FCSTD DOCUMENT  (FreeCAD 0.18R16131 (Git))
Label: letterplate_11_11
License: All rights reserved
LicenseURL: http://en.wikipedia.org/wiki/All_rights_reserved
objects: Part::Part2DObjectPython×123, Sketcher::SketchObject×1, PartDesign::Body×1, App::Part×1
note: 125 computed .brp shape members not serialized (recipe doc carries the construction recipe); baked Part::Feature solids carry a one-line shape summary decoded from their .brp

FEATURE [Sketcher::SketchObject] Sketch
  MapMode = 5
  Support = -> [XY_Plane]
FEATURE [PartDesign::Body] Body
  Group = -> [Sketch]
  Origin = -> Origin
FEATURE [Part::Part2DObjectPython] Circle  # Draft 2D object (typed FeaturePython)
  FirstAngle = 0
  LastAngle = 0
  MakeFace = true
  Placement = pos=(115,214.444,0) rot=(0,0,1;0rad)
  Radius = 2.5
FEATURE [Part::Part2DObjectPython] ShapeString  # Draft 2D object (typed FeaturePython)
  FontFile = <userpath>/Dropbox/Hobby/wordclock_git/hardware/lettering_plates/fonts/LiberationMono-Regular-stencil.ttf
  Placement = pos=(27.1303,193.241,0) rot=(0,0,1;0rad)
  Size = 11.4333
  String = H
  Tracking = 0
FEATURE [Part::Part2DObjectPython] ShapeString001  # Draft 2D object (typed FeaturePython)
  FontFile = <userpath>/Dropbox/Hobby/wordclock_git/hardware/lettering_plates/fonts/LiberationMono-Regular-stencil.ttf
  Placement = pos=(43.797,193.241,0) rot=(0,0,1;0rad)
  Size = 11.4333
  String = E
  Tracking = 0
FEATURE [Part::Part2DObjectPython] ShapeString002  # Draft 2D object (typed FeaturePython)
  FontFile = <userpath>/Dropbox/Hobby/wordclock_git/hardware/lettering_plates/fonts/LiberationMono-Regular-stencil.ttf
  Placement = pos=(60.4637,193.241,0) rot=(0,0,1;0rad)
  Size = 11.4333
  String = T
  Tracking = 0
FEATURE [Part::Part2DObjectPython] ShapeString003  # Draft 2D object (typed FeaturePython)
  FontFile = <userpath>/Dropbox/Hobby/wordclock_git/hardware/lettering_plates/fonts/LiberationMono-Regular-stencil.ttf
  Placement = pos=(77.1303,193.241,0) rot=(0,0,1;0rad)
  Size = 11.4333
  String = H
  Tracking = 0
FEATURE [Part::Part2DObjectPython] ShapeString004  # Draft 2D object (typed FeaturePython)
  FontFile = <userpath>/Dropbox/Hobby/wordclock_git/hardware/lettering_plates/fonts/LiberationMono-Regular-stencil.ttf
  Placement = pos=(93.797,193.241,0) rot=(0,0,1;0rad)
  Size = 11.4333
  String = I
  Tracking = 0
FEATURE [Part::Part2DObjectPython] ShapeString005  # Draft 2D object (typed FeaturePython)
  FontFile = <userpath>/Dropbox/Hobby/wordclock_git/hardware/lettering_plates/fonts/LiberationMono-Regular-stencil.ttf
  Placement = pos=(110.464,193.241,0) rot=(0,0,1;0rad)
  Size = 11.4333
  String = S
  Tracking = 0
FEATURE [Part::Part2DObjectPython] ShapeString006  # Draft 2D object (typed FeaturePython)
  FontFile = <userpath>/Dropbox/Hobby/wordclock_git/hardware/lettering_plates/fonts/LiberationMono-Regular-stencil.ttf
  Placement = pos=(127.13,193.241,0) rot=(0,0,1;0rad)
  Size = 11.4333
  String = B
  Tracking = 0
FEATURE [Part::Part2DObjectPython] ShapeString007  # Draft 2D object (typed FeaturePython)
  FontFile = <userpath>/Dropbox/Hobby/wordclock_git/hardware/lettering_plates/fonts/LiberationMono-Regular-stencil.ttf
  Placement = pos=(143.797,193.241,0) rot=(0,0,1;0rad)
  Size = 11.4333
  String = B
  Tracking = 0
FEATURE [Part::Part2DObjectPython] ShapeString008  # Draft 2D object (typed FeaturePython)
  FontFile = <userpath>/Dropbox/Hobby/wordclock_git/hardware/lettering_plates/fonts/LiberationMono-Regular-stencil.ttf
  Placement = pos=(160.464,193.241,0) rot=(0,0,1;0rad)
  Size = 11.4333
  String = Ĳ
  Tracking = 0
FEATURE [Part::Part2DObjectPython] ShapeString009  # Draft 2D object (typed FeaturePython)
  FontFile = <userpath>/Dropbox/Hobby/wordclock_git/hardware/lettering_plates/fonts/LiberationMono-Regular-stencil.ttf
  Placement = pos=(177.13,193.241,0) rot=(0,0,1;0rad)
  Size = 11.4333
  String = N
  Tracking = 0
FEATURE [Part::Part2DObjectPython] ShapeString010  # Draft 2D object (typed FeaturePython)
  FontFile = <userpath>/Dropbox/Hobby/wordclock_git/hardware/lettering_plates/fonts/LiberationMono-Regular-stencil.ttf
  Placement = pos=(193.797,193.241,0) rot=(0,0,1;0rad)
  Size = 11.4333
  String = A
  Tracking = 0
FEATURE [Part::Part2DObjectPython] ShapeString011  # Draft 2D object (typed FeaturePython)
  FontFile = <userpath>/Dropbox/Hobby/wordclock_git/hardware/lettering_plates/fonts/LiberationMono-Regular-stencil.ttf
  Placement = pos=(27.1303,176.574,0) rot=(0,0,1;0rad)
  Size = 11.4333
  String = N
  Tracking = 0
FEATURE [Part::Part2DObjectPython] ShapeString012  # Draft 2D object (typed FeaturePython)
  FontFile = <userpath>/Dropbox/Hobby/wordclock_git/hardware/lettering_plates/fonts/LiberationMono-Regular-stencil.ttf
  Placement = pos=(43.797,176.574,0) rot=(0,0,1;0rad)
  Size = 11.4333
  String = U
  Tracking = 0
FEATURE [Part::Part2DObjectPython] ShapeString013  # Draft 2D object (typed FeaturePython)
  FontFile = <userpath>/Dropbox/Hobby/wordclock_git/hardware/lettering_plates/fonts/LiberationMono-Regular-stencil.ttf
  Placement = pos=(60.4637,176.574,0) rot=(0,0,1;0rad)
  Size = 11.4333
  String = S
  Tracking = 0
FEATURE [Part::Part2DObjectPython] ShapeString014  # Draft 2D object (typed FeaturePython)
  FontFile = <userpath>/Dropbox/Hobby/wordclock_git/hardware/lettering_plates/fonts/LiberationMono-Regular-stencil.ttf
  Placement = pos=(77.1303,176.574,0) rot=(0,0,1;0rad)
  Size = 11.4333
  String = K
  Tracking = 0
FEATURE [Part::Part2DObjectPython] ShapeString015  # Draft 2D object (typed FeaturePython)
  FontFile = <userpath>/Dropbox/Hobby/wordclock_git/hardware/lettering_plates/fonts/LiberationMono-Regular-stencil.ttf
  Placement = pos=(93.797,176.574,0) rot=(0,0,1;0rad)
  Size = 11.4333
  String = W
  Tracking = 0
FEATURE [Part::Part2DObjectPython] ShapeString016  # Draft 2D object (typed FeaturePython)
  FontFile = <userpath>/Dropbox/Hobby/wordclock_git/hardware/lettering_plates/fonts/LiberationMono-Regular-stencil.ttf
  Placement = pos=(110.464,176.574,0) rot=(0,0,1;0rad)
  Size = 11.4333
  String = A
  Tracking = 0
FEATURE [Part::Part2DObjectPython] ShapeString017  # Draft 2D object (typed FeaturePython)
  FontFile = <userpath>/Dropbox/Hobby/wordclock_git/hardware/lettering_plates/fonts/LiberationMono-Regular-stencil.ttf
  Placement = pos=(127.13,176.574,0) rot=(0,0,1;0rad)
  Size = 11.4333
  String = R
  Tracking = 0
FEATURE [Part::Part2DObjectPython] ShapeString018  # Draft 2D object (typed FeaturePython)
  FontFile = <userpath>/Dropbox/Hobby/wordclock_git/hardware/lettering_plates/fonts/LiberationMono-Regular-stencil.ttf
  Placement = pos=(143.797,176.574,0) rot=(0,0,1;0rad)
  Size = 11.4333
  String = T
  Tracking = 0
FEATURE [Part::Part2DObjectPython] ShapeString019  # Draft 2D object (typed FeaturePython)
  FontFile = <userpath>/Dropbox/Hobby/wordclock_git/hardware/lettering_plates/fonts/LiberationMono-Regular-stencil.ttf
  Placement = pos=(160.464,176.574,0) rot=(0,0,1;0rad)
  Size = 11.4333
  String = I
  Tracking = 0
FEATURE [Part::Part2DObjectPython] ShapeString020  # Draft 2D object (typed FeaturePython)
  FontFile = <userpath>/Dropbox/Hobby/wordclock_git/hardware/lettering_plates/fonts/LiberationMono-Regular-stencil.ttf
  Placement = pos=(177.13,176.574,0) rot=(0,0,1;0rad)
  Size = 11.4333
  String = E
  Tracking = 0
FEATURE [Part::Part2DObjectPython] ShapeString021  # Draft 2D object (typed FeaturePython)
  FontFile = <userpath>/Dropbox/Hobby/wordclock_git/hardware/lettering_plates/fonts/LiberationMono-Regular-stencil.ttf
  Placement = pos=(193.797,176.574,0) rot=(0,0,1;0rad)
  Size = 11.4333
  String = N
  Tracking = 0
FEATURE [Part::Part2DObjectPython] ShapeString022  # Draft 2D object (typed FeaturePython)
  FontFile = <userpath>/Dropbox/Hobby/wordclock_git/hardware/lettering_plates/fonts/LiberationMono-Regular-stencil.ttf
  Placement = pos=(27.1303,159.908,0) rot=(0,0,1;0rad)
  Size = 11.4333
  String = V
  Tracking = 0
FEATURE [Part::Part2DObjectPython] ShapeString023  # Draft 2D object (typed FeaturePython)
  FontFile = <userpath>/Dropbox/Hobby/wordclock_git/hardware/lettering_plates/fonts/LiberationMono-Regular-stencil.ttf
  Placement = pos=(43.797,159.908,0) rot=(0,0,1;0rad)
  Size = 11.4333
  String = I
  Tracking = 0
FEATURE [Part::Part2DObjectPython] ShapeString024  # Draft 2D object (typed FeaturePython)
  FontFile = <userpath>/Dropbox/Hobby/wordclock_git/hardware/lettering_plates/fonts/LiberationMono-Regular-stencil.ttf
  Placement = pos=(60.4637,159.908,0) rot=(0,0,1;0rad)
  Size = 11.4333
  String = J
  Tracking = 0
FEATURE [Part::Part2DObjectPython] ShapeString025  # Draft 2D object (typed FeaturePython)
  FontFile = <userpath>/Dropbox/Hobby/wordclock_git/hardware/lettering_plates/fonts/LiberationMono-Regular-stencil.ttf
  Placement = pos=(77.1303,159.908,0) rot=(0,0,1;0rad)
  Size = 11.4333
  String = F
  Tracking = 0
FEATURE [Part::Part2DObjectPython] ShapeString026  # Draft 2D object (typed FeaturePython)
  FontFile = <userpath>/Dropbox/Hobby/wordclock_git/hardware/lettering_plates/fonts/LiberationMono-Regular-stencil.ttf
  Placement = pos=(93.797,159.908,0) rot=(0,0,1;0rad)
  Size = 11.4333
  String = X
  Tracking = 0
FEATURE [Part::Part2DObjectPython] ShapeString027  # Draft 2D object (typed FeaturePython)
  FontFile = <userpath>/Dropbox/Hobby/wordclock_git/hardware/lettering_plates/fonts/LiberationMono-Regular-stencil.ttf
  Placement = pos=(110.464,159.908,0) rot=(0,0,1;0rad)
  Size = 11.4333
  String = R
  Tracking = 0
FEATURE [Part::Part2DObjectPython] ShapeString028  # Draft 2D object (typed FeaturePython)
  FontFile = <userpath>/Dropbox/Hobby/wordclock_git/hardware/lettering_plates/fonts/LiberationMono-Regular-stencil.ttf
  Placement = pos=(127.13,159.908,0) rot=(0,0,1;0rad)
  Size = 11.4333
  String = V
  Tracking = 0
FEATURE [Part::Part2DObjectPython] ShapeString029  # Draft 2D object (typed FeaturePython)
  FontFile = <userpath>/Dropbox/Hobby/wordclock_git/hardware/lettering_plates/fonts/LiberationMono-Regular-stencil.ttf
  Placement = pos=(143.797,159.908,0) rot=(0,0,1;0rad)
  Size = 11.4333
  String = O
  Tracking = 0
FEATURE [Part::Part2DObjectPython] ShapeString030  # Draft 2D object (typed FeaturePython)
  FontFile = <userpath>/Dropbox/Hobby/wordclock_git/hardware/lettering_plates/fonts/LiberationMono-Regular-stencil.ttf
  Placement = pos=(160.464,159.908,0) rot=(0,0,1;0rad)
  Size = 11.4333
  String = O
  Tracking = 0
FEATURE [Part::Part2DObjectPython] ShapeString031  # Draft 2D object (typed FeaturePython)
  FontFile = <userpath>/Dropbox/Hobby/wordclock_git/hardware/lettering_plates/fonts/LiberationMono-Regular-stencil.ttf
  Placement = pos=(177.13,159.908,0) rot=(0,0,1;0rad)
  Size = 11.4333
  String = R
  Tracking = 0
FEATURE [Part::Part2DObjectPython] ShapeString032  # Draft 2D object (typed FeaturePython)
  FontFile = <userpath>/Dropbox/Hobby/wordclock_git/hardware/lettering_plates/fonts/LiberationMono-Regular-stencil.ttf
  Placement = pos=(193.797,159.908,0) rot=(0,0,1;0rad)
  Size = 11.4333
  String = N
  Tracking = 0
FEATURE [Part::Part2DObjectPython] ShapeString033  # Draft 2D object (typed FeaturePython)
  FontFile = <userpath>/Dropbox/Hobby/wordclock_git/hardware/lettering_plates/fonts/LiberationMono-Regular-stencil.ttf
  Placement = pos=(27.1303,143.241,0) rot=(0,0,1;0rad)
  Size = 11.4333
  String = O
  Tracking = 0
FEATURE [Part::Part2DObjectPython] ShapeString034  # Draft 2D object (typed FeaturePython)
  FontFile = <userpath>/Dropbox/Hobby/wordclock_git/hardware/lettering_plates/fonts/LiberationMono-Regular-stencil.ttf
  Placement = pos=(43.797,143.241,0) rot=(0,0,1;0rad)
  Size = 11.4333
  String = V
  Tracking = 0
FEATURE [Part::Part2DObjectPython] ShapeString035  # Draft 2D object (typed FeaturePython)
  FontFile = <userpath>/Dropbox/Hobby/wordclock_git/hardware/lettering_plates/fonts/LiberationMono-Regular-stencil.ttf
  Placement = pos=(60.4637,143.241,0) rot=(0,0,1;0rad)
  Size = 11.4333
  String = E
  Tracking = 0
FEATURE [Part::Part2DObjectPython] ShapeString036  # Draft 2D object (typed FeaturePython)
  FontFile = <userpath>/Dropbox/Hobby/wordclock_git/hardware/lettering_plates/fonts/LiberationMono-Regular-stencil.ttf
  Placement = pos=(77.1303,143.241,0) rot=(0,0,1;0rad)
  Size = 11.4333
  String = R
  Tracking = 0
FEATURE [Part::Part2DObjectPython] ShapeString037  # Draft 2D object (typed FeaturePython)
  FontFile = <userpath>/Dropbox/Hobby/wordclock_git/hardware/lettering_plates/fonts/LiberationMono-Regular-stencil.ttf
  Placement = pos=(93.797,143.241,0) rot=(0,0,1;0rad)
  Size = 11.4333
  String = X
  Tracking = 0
FEATURE [Part::Part2DObjectPython] ShapeString038  # Draft 2D object (typed FeaturePython)
  FontFile = <userpath>/Dropbox/Hobby/wordclock_git/hardware/lettering_plates/fonts/LiberationMono-Regular-stencil.ttf
  Placement = pos=(110.464,143.241,0) rot=(0,0,1;0rad)
  Size = 11.4333
  String = Z
  Tracking = 0
FEATURE [Part::Part2DObjectPython] ShapeString039  # Draft 2D object (typed FeaturePython)
  FontFile = <userpath>/Dropbox/Hobby/wordclock_git/hardware/lettering_plates/fonts/LiberationMono-Regular-stencil.ttf
  Placement = pos=(127.13,143.241,0) rot=(0,0,1;0rad)
  Size = 11.4333
  String = H
  Tracking = 0
FEATURE [Part::Part2DObjectPython] ShapeString040  # Draft 2D object (typed FeaturePython)
  FontFile = <userpath>/Dropbox/Hobby/wordclock_git/hardware/lettering_plates/fonts/LiberationMono-Regular-stencil.ttf
  Placement = pos=(143.797,143.241,0) rot=(0,0,1;0rad)
  Size = 11.4333
  String = A
  Tracking = 0
FEATURE [Part::Part2DObjectPython] ShapeString041  # Draft 2D object (typed FeaturePython)
  FontFile = <userpath>/Dropbox/Hobby/wordclock_git/hardware/lettering_plates/fonts/LiberationMono-Regular-stencil.ttf
  Placement = pos=(160.464,143.241,0) rot=(0,0,1;0rad)
  Size = 11.4333
  String = L
  Tracking = 0
FEATURE [Part::Part2DObjectPython] ShapeString042  # Draft 2D object (typed FeaturePython)
  FontFile = <userpath>/Dropbox/Hobby/wordclock_git/hardware/lettering_plates/fonts/LiberationMono-Regular-stencil.ttf
  Placement = pos=(177.13,143.241,0) rot=(0,0,1;0rad)
  Size = 11.4333
  String = F
  Tracking = 0
FEATURE [Part::Part2DObjectPython] ShapeString043  # Draft 2D object (typed FeaturePython)
  FontFile = <userpath>/Dropbox/Hobby/wordclock_git/hardware/lettering_plates/fonts/LiberationMono-Regular-stencil.ttf
  Placement = pos=(193.797,143.241,0) rot=(0,0,1;0rad)
  Size = 11.4333
  String = D
  Tracking = 0
FEATURE [Part::Part2DObjectPython] ShapeString044  # Draft 2D object (typed FeaturePython)
  FontFile = <userpath>/Dropbox/Hobby/wordclock_git/hardware/lettering_plates/fonts/LiberationMono-Regular-stencil.ttf
  Placement = pos=(27.1303,126.574,0) rot=(0,0,1;0rad)
  Size = 11.4333
  String = Z
  Tracking = 0
FEATURE [Part::Part2DObjectPython] ShapeString045  # Draft 2D object (typed FeaturePython)
  FontFile = <userpath>/Dropbox/Hobby/wordclock_git/hardware/lettering_plates/fonts/LiberationMono-Regular-stencil.ttf
  Placement = pos=(43.797,126.574,0) rot=(0,0,1;0rad)
  Size = 11.4333
  String = E
  Tracking = 0
FEATURE [Part::Part2DObjectPython] ShapeString046  # Draft 2D object (typed FeaturePython)
  FontFile = <userpath>/Dropbox/Hobby/wordclock_git/hardware/lettering_plates/fonts/LiberationMono-Regular-stencil.ttf
  Placement = pos=(60.4637,126.574,0) rot=(0,0,1;0rad)
  Size = 11.4333
  String = S
  Tracking = 0
FEATURE [Part::Part2DObjectPython] ShapeString047  # Draft 2D object (typed FeaturePython)
  FontFile = <userpath>/Dropbox/Hobby/wordclock_git/hardware/lettering_plates/fonts/LiberationMono-Regular-stencil.ttf
  Placement = pos=(77.1303,126.574,0) rot=(0,0,1;0rad)
  Size = 11.4333
  String = T
  Tracking = 0
FEATURE [Part::Part2DObjectPython] ShapeString048  # Draft 2D object (typed FeaturePython)
  FontFile = <userpath>/Dropbox/Hobby/wordclock_git/hardware/lettering_plates/fonts/LiberationMono-Regular-stencil.ttf
  Placement = pos=(93.797,126.574,0) rot=(0,0,1;0rad)
  Size = 11.4333
  String = W
  Tracking = 0
FEATURE [Part::Part2DObjectPython] ShapeString049  # Draft 2D object (typed FeaturePython)
  FontFile = <userpath>/Dropbox/Hobby/wordclock_git/hardware/lettering_plates/fonts/LiberationMono-Regular-stencil.ttf
  Placement = pos=(110.464,126.574,0) rot=(0,0,1;0rad)
  Size = 11.4333
  String = A
  Tracking = 0
FEATURE [Part::Part2DObjectPython] ShapeString050  # Draft 2D object (typed FeaturePython)
  FontFile = <userpath>/Dropbox/Hobby/wordclock_git/hardware/lettering_plates/fonts/LiberationMono-Regular-stencil.ttf
  Placement = pos=(127.13,126.574,0) rot=(0,0,1;0rad)
  Size = 11.4333
  String = A
  Tracking = 0
FEATURE [Part::Part2DObjectPython] ShapeString051  # Draft 2D object (typed FeaturePython)
  FontFile = <userpath>/Dropbox/Hobby/wordclock_git/hardware/lettering_plates/fonts/LiberationMono-Regular-stencil.ttf
  Placement = pos=(143.797,126.574,0) rot=(0,0,1;0rad)
  Size = 11.4333
  String = L
  Tracking = 0
FEATURE [Part::Part2DObjectPython] ShapeString052  # Draft 2D object (typed FeaturePython)
  FontFile = <userpath>/Dropbox/Hobby/wordclock_git/hardware/lettering_plates/fonts/LiberationMono-Regular-stencil.ttf
  Placement = pos=(160.464,126.574,0) rot=(0,0,1;0rad)
  Size = 11.4333
  String = F
  Tracking = 0
FEATURE [Part::Part2DObjectPython] ShapeString053  # Draft 2D object (typed FeaturePython)
  FontFile = <userpath>/Dropbox/Hobby/wordclock_git/hardware/lettering_plates/fonts/LiberationMono-Regular-stencil.ttf
  Placement = pos=(177.13,126.574,0) rot=(0,0,1;0rad)
  Size = 11.4333
  String = S
  Tracking = 0
FEATURE [Part::Part2DObjectPython] ShapeString054  # Draft 2D object (typed FeaturePython)
  FontFile = <userpath>/Dropbox/Hobby/wordclock_git/hardware/lettering_plates/fonts/LiberationMono-Regular-stencil.ttf
  Placement = pos=(193.797,126.574,0) rot=(0,0,1;0rad)
  Size = 11.4333
  String = E
  Tracking = 0
FEATURE [Part::Part2DObjectPython] ShapeString055  # Draft 2D object (typed FeaturePython)
  FontFile = <userpath>/Dropbox/Hobby/wordclock_git/hardware/lettering_plates/fonts/LiberationMono-Regular-stencil.ttf
  Placement = pos=(27.1303,109.908,0) rot=(0,0,1;0rad)
  Size = 11.4333
  String = D
  Tracking = 0
FEATURE [Part::Part2DObjectPython] ShapeString056  # Draft 2D object (typed FeaturePython)
  FontFile = <userpath>/Dropbox/Hobby/wordclock_git/hardware/lettering_plates/fonts/LiberationMono-Regular-stencil.ttf
  Placement = pos=(43.797,109.908,0) rot=(0,0,1;0rad)
  Size = 11.4333
  String = R
  Tracking = 0
FEATURE [Part::Part2DObjectPython] ShapeString057  # Draft 2D object (typed FeaturePython)
  FontFile = <userpath>/Dropbox/Hobby/wordclock_git/hardware/lettering_plates/fonts/LiberationMono-Regular-stencil.ttf
  Placement = pos=(60.4637,109.908,0) rot=(0,0,1;0rad)
  Size = 11.4333
  String = I
  Tracking = 0
FEATURE [Part::Part2DObjectPython] ShapeString058  # Draft 2D object (typed FeaturePython)
  FontFile = <userpath>/Dropbox/Hobby/wordclock_git/hardware/lettering_plates/fonts/LiberationMono-Regular-stencil.ttf
  Placement = pos=(77.1303,109.908,0) rot=(0,0,1;0rad)
  Size = 11.4333
  String = E
  Tracking = 0
FEATURE [Part::Part2DObjectPython] ShapeString059  # Draft 2D object (typed FeaturePython)
  FontFile = <userpath>/Dropbox/Hobby/wordclock_git/hardware/lettering_plates/fonts/LiberationMono-Regular-stencil.ttf
  Placement = pos=(93.797,109.908,0) rot=(0,0,1;0rad)
  Size = 11.4333
  String = V
  Tracking = 0
FEATURE [Part::Part2DObjectPython] ShapeString060  # Draft 2D object (typed FeaturePython)
  FontFile = <userpath>/Dropbox/Hobby/wordclock_git/hardware/lettering_plates/fonts/LiberationMono-Regular-stencil.ttf
  Placement = pos=(110.464,109.908,0) rot=(0,0,1;0rad)
  Size = 11.4333
  String = I
  Tracking = 0
FEATURE [Part::Part2DObjectPython] ShapeString061  # Draft 2D object (typed FeaturePython)
  FontFile = <userpath>/Dropbox/Hobby/wordclock_git/hardware/lettering_plates/fonts/LiberationMono-Regular-stencil.ttf
  Placement = pos=(127.13,109.908,0) rot=(0,0,1;0rad)
  Size = 11.4333
  String = E
  Tracking = 0
FEATURE [Part::Part2DObjectPython] ShapeString062  # Draft 2D object (typed FeaturePython)
  FontFile = <userpath>/Dropbox/Hobby/wordclock_git/hardware/lettering_plates/fonts/LiberationMono-Regular-stencil.ttf
  Placement = pos=(143.797,109.908,0) rot=(0,0,1;0rad)
  Size = 11.4333
  String = R
  Tracking = 0
FEATURE [Part::Part2DObjectPython] ShapeString063  # Draft 2D object (typed FeaturePython)
  FontFile = <userpath>/Dropbox/Hobby/wordclock_git/hardware/lettering_plates/fonts/LiberationMono-Regular-stencil.ttf
  Placement = pos=(160.464,109.908,0) rot=(0,0,1;0rad)
  Size = 11.4333
  String = E
  Tracking = 0
FEATURE [Part::Part2DObjectPython] ShapeString064  # Draft 2D object (typed FeaturePython)
  FontFile = <userpath>/Dropbox/Hobby/wordclock_git/hardware/lettering_plates/fonts/LiberationMono-Regular-stencil.ttf
  Placement = pos=(177.13,109.908,0) rot=(0,0,1;0rad)
  Size = 11.4333
  String = E
  Tracking = 0
FEATURE [Part::Part2DObjectPython] ShapeString065  # Draft 2D object (typed FeaturePython)
  FontFile = <userpath>/Dropbox/Hobby/wordclock_git/hardware/lettering_plates/fonts/LiberationMono-Regular-stencil.ttf
  Placement = pos=(193.797,109.908,0) rot=(0,0,1;0rad)
  Size = 11.4333
  String = N
  Tracking = 0
FEATURE [Part::Part2DObjectPython] ShapeString066  # Draft 2D object (typed FeaturePython)
  FontFile = <userpath>/Dropbox/Hobby/wordclock_git/hardware/lettering_plates/fonts/LiberationMono-Regular-stencil.ttf
  Placement = pos=(27.1303,93.2409,0) rot=(0,0,1;0rad)
  Size = 11.4333
  String = T
  Tracking = 0
FEATURE [Part::Part2DObjectPython] ShapeString067  # Draft 2D object (typed FeaturePython)
  FontFile = <userpath>/Dropbox/Hobby/wordclock_git/hardware/lettering_plates/fonts/LiberationMono-Regular-stencil.ttf
  Placement = pos=(43.797,93.2409,0) rot=(0,0,1;0rad)
  Size = 11.4333
  String = W
  Tracking = 0
FEATURE [Part::Part2DObjectPython] ShapeString068  # Draft 2D object (typed FeaturePython)
  FontFile = <userpath>/Dropbox/Hobby/wordclock_git/hardware/lettering_plates/fonts/LiberationMono-Regular-stencil.ttf
  Placement = pos=(60.4637,93.2409,0) rot=(0,0,1;0rad)
  Size = 11.4333
  String = E
  Tracking = 0
FEATURE [Part::Part2DObjectPython] ShapeString069  # Draft 2D object (typed FeaturePython)
  FontFile = <userpath>/Dropbox/Hobby/wordclock_git/hardware/lettering_plates/fonts/LiberationMono-Regular-stencil.ttf
  Placement = pos=(77.1303,93.2409,0) rot=(0,0,1;0rad)
  Size = 11.4333
  String = E
  Tracking = 0
FEATURE [Part::Part2DObjectPython] ShapeString070  # Draft 2D object (typed FeaturePython)
  FontFile = <userpath>/Dropbox/Hobby/wordclock_git/hardware/lettering_plates/fonts/LiberationMono-Regular-stencil.ttf
  Placement = pos=(93.797,93.2409,0) rot=(0,0,1;0rad)
  Size = 11.4333
  String = E
  Tracking = 0
FEATURE [Part::Part2DObjectPython] ShapeString071  # Draft 2D object (typed FeaturePython)
  FontFile = <userpath>/Dropbox/Hobby/wordclock_git/hardware/lettering_plates/fonts/LiberationMono-Regular-stencil.ttf
  Placement = pos=(110.464,93.2409,0) rot=(0,0,1;0rad)
  Size = 11.4333
  String = W
  Tracking = 0
FEATURE [Part::Part2DObjectPython] ShapeString072  # Draft 2D object (typed FeaturePython)
  FontFile = <userpath>/Dropbox/Hobby/wordclock_git/hardware/lettering_plates/fonts/LiberationMono-Regular-stencil.ttf
  Placement = pos=(127.13,93.2409,0) rot=(0,0,1;0rad)
  Size = 11.4333
  String = A
  Tracking = 0
FEATURE [Part::Part2DObjectPython] ShapeString073  # Draft 2D object (typed FeaturePython)
  FontFile = <userpath>/Dropbox/Hobby/wordclock_git/hardware/lettering_plates/fonts/LiberationMono-Regular-stencil.ttf
  Placement = pos=(143.797,93.2409,0) rot=(0,0,1;0rad)
  Size = 11.4333
  String = C
  Tracking = 0
FEATURE [Part::Part2DObjectPython] ShapeString074  # Draft 2D object (typed FeaturePython)
  FontFile = <userpath>/Dropbox/Hobby/wordclock_git/hardware/lettering_plates/fonts/LiberationMono-Regular-stencil.ttf
  Placement = pos=(160.464,93.2409,0) rot=(0,0,1;0rad)
  Size = 11.4333
  String = H
  Tracking = 0
FEATURE [Part::Part2DObjectPython] ShapeString075  # Draft 2D object (typed FeaturePython)
  FontFile = <userpath>/Dropbox/Hobby/wordclock_git/hardware/lettering_plates/fonts/LiberationMono-Regular-stencil.ttf
  Placement = pos=(177.13,93.2409,0) rot=(0,0,1;0rad)
  Size = 11.4333
  String = T
  Tracking = 0
FEATURE [Part::Part2DObjectPython] ShapeString076  # Draft 2D object (typed FeaturePython)
  FontFile = <userpath>/Dropbox/Hobby/wordclock_git/hardware/lettering_plates/fonts/LiberationMono-Regular-stencil.ttf
  Placement = pos=(193.797,93.2409,0) rot=(0,0,1;0rad)
  Size = 11.4333
  String = R
  Tracking = 0
FEATURE [Part::Part2DObjectPython] ShapeString077  # Draft 2D object (typed FeaturePython)
  FontFile = <userpath>/Dropbox/Hobby/wordclock_git/hardware/lettering_plates/fonts/LiberationMono-Regular-stencil.ttf
  Placement = pos=(27.1303,76.5742,0) rot=(0,0,1;0rad)
  Size = 11.4333
  String = Z
  Tracking = 0
FEATURE [Part::Part2DObjectPython] ShapeString078  # Draft 2D object (typed FeaturePython)
  FontFile = <userpath>/Dropbox/Hobby/wordclock_git/hardware/lettering_plates/fonts/LiberationMono-Regular-stencil.ttf
  Placement = pos=(43.797,76.5742,0) rot=(0,0,1;0rad)
  Size = 11.4333
  String = E
  Tracking = 0
FEATURE [Part::Part2DObjectPython] ShapeString079  # Draft 2D object (typed FeaturePython)
  FontFile = <userpath>/Dropbox/Hobby/wordclock_git/hardware/lettering_plates/fonts/LiberationMono-Regular-stencil.ttf
  Placement = pos=(60.4637,76.5742,0) rot=(0,0,1;0rad)
  Size = 11.4333
  String = V
  Tracking = 0
FEATURE [Part::Part2DObjectPython] ShapeString080  # Draft 2D object (typed FeaturePython)
  FontFile = <userpath>/Dropbox/Hobby/wordclock_git/hardware/lettering_plates/fonts/LiberationMono-Regular-stencil.ttf
  Placement = pos=(77.1303,76.5742,0) rot=(0,0,1;0rad)
  Size = 11.4333
  String = E
  Tracking = 0
FEATURE [Part::Part2DObjectPython] ShapeString081  # Draft 2D object (typed FeaturePython)
  FontFile = <userpath>/Dropbox/Hobby/wordclock_git/hardware/lettering_plates/fonts/LiberationMono-Regular-stencil.ttf
  Placement = pos=(93.797,76.5742,0) rot=(0,0,1;0rad)
  Size = 11.4333
  String = N
  Tracking = 0
FEATURE [Part::Part2DObjectPython] ShapeString082  # Draft 2D object (typed FeaturePython)
  FontFile = <userpath>/Dropbox/Hobby/wordclock_git/hardware/lettering_plates/fonts/LiberationMono-Regular-stencil.ttf
  Placement = pos=(110.464,76.5742,0) rot=(0,0,1;0rad)
  Size = 11.4333
  String = E
  Tracking = 0
FEATURE [Part::Part2DObjectPython] ShapeString083  # Draft 2D object (typed FeaturePython)
  FontFile = <userpath>/Dropbox/Hobby/wordclock_git/hardware/lettering_plates/fonts/LiberationMono-Regular-stencil.ttf
  Placement = pos=(127.13,76.5742,0) rot=(0,0,1;0rad)
  Size = 11.4333
  String = G
  Tracking = 0
FEATURE [Part::Part2DObjectPython] ShapeString084  # Draft 2D object (typed FeaturePython)
  FontFile = <userpath>/Dropbox/Hobby/wordclock_git/hardware/lettering_plates/fonts/LiberationMono-Regular-stencil.ttf
  Placement = pos=(143.797,76.5742,0) rot=(0,0,1;0rad)
  Size = 11.4333
  String = E
  Tracking = 0
FEATURE [Part::Part2DObjectPython] ShapeString085  # Draft 2D object (typed FeaturePython)
  FontFile = <userpath>/Dropbox/Hobby/wordclock_git/hardware/lettering_plates/fonts/LiberationMono-Regular-stencil.ttf
  Placement = pos=(160.464,76.5742,0) rot=(0,0,1;0rad)
  Size = 11.4333
  String = N
  Tracking = 0
FEATURE [Part::Part2DObjectPython] ShapeString086  # Draft 2D object (typed FeaturePython)
  FontFile = <userpath>/Dropbox/Hobby/wordclock_git/hardware/lettering_plates/fonts/LiberationMono-Regular-stencil.ttf
  Placement = pos=(177.13,76.5742,0) rot=(0,0,1;0rad)
  Size = 11.4333
  String = B
  Tracking = 0
FEATURE [Part::Part2DObjectPython] ShapeString087  # Draft 2D object (typed FeaturePython)
  FontFile = <userpath>/Dropbox/Hobby/wordclock_git/hardware/lettering_plates/fonts/LiberationMono-Regular-stencil.ttf
  Placement = pos=(193.797,76.5742,0) rot=(0,0,1;0rad)
  Size = 11.4333
  String = M
  Tracking = 0
FEATURE [Part::Part2DObjectPython] ShapeString088  # Draft 2D object (typed FeaturePython)
  FontFile = <userpath>/Dropbox/Hobby/wordclock_git/hardware/lettering_plates/fonts/LiberationMono-Regular-stencil.ttf
  Placement = pos=(27.1303,59.9075,0) rot=(0,0,1;0rad)
  Size = 11.4333
  String = T
  Tracking = 0
FEATURE [Part::Part2DObjectPython] ShapeString089  # Draft 2D object (typed FeaturePython)
  FontFile = <userpath>/Dropbox/Hobby/wordclock_git/hardware/lettering_plates/fonts/LiberationMono-Regular-stencil.ttf
  Placement = pos=(43.797,59.9075,0) rot=(0,0,1;0rad)
  Size = 11.4333
  String = I
  Tracking = 0
FEATURE [Part::Part2DObjectPython] ShapeString090  # Draft 2D object (typed FeaturePython)
  FontFile = <userpath>/Dropbox/Hobby/wordclock_git/hardware/lettering_plates/fonts/LiberationMono-Regular-stencil.ttf
  Placement = pos=(60.4637,59.9075,0) rot=(0,0,1;0rad)
  Size = 11.4333
  String = E
  Tracking = 0
FEATURE [Part::Part2DObjectPython] ShapeString091  # Draft 2D object (typed FeaturePython)
  FontFile = <userpath>/Dropbox/Hobby/wordclock_git/hardware/lettering_plates/fonts/LiberationMono-Regular-stencil.ttf
  Placement = pos=(77.1303,59.9075,0) rot=(0,0,1;0rad)
  Size = 11.4333
  String = N
  Tracking = 0
FEATURE [Part::Part2DObjectPython] ShapeString092  # Draft 2D object (typed FeaturePython)
  FontFile = <userpath>/Dropbox/Hobby/wordclock_git/hardware/lettering_plates/fonts/LiberationMono-Regular-stencil.ttf
  Placement = pos=(93.797,59.9075,0) rot=(0,0,1;0rad)
  Size = 11.4333
  String = E
  Tracking = 0
FEATURE [Part::Part2DObjectPython] ShapeString093  # Draft 2D object (typed FeaturePython)
  FontFile = <userpath>/Dropbox/Hobby/wordclock_git/hardware/lettering_plates/fonts/LiberationMono-Regular-stencil.ttf
  Placement = pos=(110.464,59.9075,0) rot=(0,0,1;0rad)
  Size = 11.4333
  String = L
  Tracking = 0
FEATURE [Part::Part2DObjectPython] ShapeString094  # Draft 2D object (typed FeaturePython)
  FontFile = <userpath>/Dropbox/Hobby/wordclock_git/hardware/lettering_plates/fonts/LiberationMono-Regular-stencil.ttf
  Placement = pos=(127.13,59.9075,0) rot=(0,0,1;0rad)
  Size = 11.4333
  String = F
  Tracking = 0
FEATURE [Part::Part2DObjectPython] ShapeString095  # Draft 2D object (typed FeaturePython)
  FontFile = <userpath>/Dropbox/Hobby/wordclock_git/hardware/lettering_plates/fonts/LiberationMono-Regular-stencil.ttf
  Placement = pos=(143.797,59.9075,0) rot=(0,0,1;0rad)
  Size = 11.4333
  String = V
  Tracking = 0
FEATURE [Part::Part2DObjectPython] ShapeString096  # Draft 2D object (typed FeaturePython)
  FontFile = <userpath>/Dropbox/Hobby/wordclock_git/hardware/lettering_plates/fonts/LiberationMono-Regular-stencil.ttf
  Placement = pos=(160.464,59.9075,0) rot=(0,0,1;0rad)
  Size = 11.4333
  String = I
  Tracking = 0
FEATURE [Part::Part2DObjectPython] ShapeString097  # Draft 2D object (typed FeaturePython)
  FontFile = <userpath>/Dropbox/Hobby/wordclock_git/hardware/lettering_plates/fonts/LiberationMono-Regular-stencil.ttf
  Placement = pos=(177.13,59.9075,0) rot=(0,0,1;0rad)
  Size = 11.4333
  String = J
  Tracking = 0
FEATURE [Part::Part2DObjectPython] ShapeString098  # Draft 2D object (typed FeaturePython)
  FontFile = <userpath>/Dropbox/Hobby/wordclock_git/hardware/lettering_plates/fonts/LiberationMono-Regular-stencil.ttf
  Placement = pos=(193.797,59.9075,0) rot=(0,0,1;0rad)
  Size = 11.4333
  String = F
  Tracking = 0
FEATURE [Part::Part2DObjectPython] ShapeString099  # Draft 2D object (typed FeaturePython)
  FontFile = <userpath>/Dropbox/Hobby/wordclock_git/hardware/lettering_plates/fonts/LiberationMono-Regular-stencil.ttf
  Placement = pos=(27.1303,43.2409,0) rot=(0,0,1;0rad)
  Size = 11.4333
  String = C
  Tracking = 0
FEATURE [Part::Part2DObjectPython] ShapeString100  # Draft 2D object (typed FeaturePython)
  FontFile = <userpath>/Dropbox/Hobby/wordclock_git/hardware/lettering_plates/fonts/LiberationMono-Regular-stencil.ttf
  Placement = pos=(43.797,43.2409,0) rot=(0,0,1;0rad)
  Size = 11.4333
  String = U
  Tracking = 0
FEATURE [Part::Part2DObjectPython] ShapeString101  # Draft 2D object (typed FeaturePython)
  FontFile = <userpath>/Dropbox/Hobby/wordclock_git/hardware/lettering_plates/fonts/LiberationMono-Regular-stencil.ttf
  Placement = pos=(60.4637,43.2409,0) rot=(0,0,1;0rad)
  Size = 11.4333
  String = U
  Tracking = 0
FEATURE [Part::Part2DObjectPython] ShapeString102  # Draft 2D object (typed FeaturePython)
  FontFile = <userpath>/Dropbox/Hobby/wordclock_git/hardware/lettering_plates/fonts/LiberationMono-Regular-stencil.ttf
  Placement = pos=(77.1303,43.2409,0) rot=(0,0,1;0rad)
  Size = 11.4333
  String = R
  Tracking = 0
FEATURE [Part::Part2DObjectPython] ShapeString103  # Draft 2D object (typed FeaturePython)
  FontFile = <userpath>/Dropbox/Hobby/wordclock_git/hardware/lettering_plates/fonts/LiberationMono-Regular-stencil.ttf
  Placement = pos=(93.797,43.2409,0) rot=(0,0,1;0rad)
  Size = 11.4333
  String = L
  Tracking = 0
FEATURE [Part::Part2DObjectPython] ShapeString104  # Draft 2D object (typed FeaturePython)
  FontFile = <userpath>/Dropbox/Hobby/wordclock_git/hardware/lettering_plates/fonts/LiberationMono-Regular-stencil.ttf
  Placement = pos=(110.464,43.2409,0) rot=(0,0,1;0rad)
  Size = 11.4333
  String = B
  Tracking = 0
FEATURE [Part::Part2DObjectPython] ShapeString105  # Draft 2D object (typed FeaturePython)
  FontFile = <userpath>/Dropbox/Hobby/wordclock_git/hardware/lettering_plates/fonts/LiberationMono-Regular-stencil.ttf
  Placement = pos=(127.13,43.2409,0) rot=(0,0,1;0rad)
  Size = 11.4333
  String = Y
  Tracking = 0
FEATURE [Part::Part2DObjectPython] ShapeString106  # Draft 2D object (typed FeaturePython)
  FontFile = <userpath>/Dropbox/Hobby/wordclock_git/hardware/lettering_plates/fonts/LiberationMono-Regular-stencil.ttf
  Placement = pos=(143.797,43.2409,0) rot=(0,0,1;0rad)
  Size = 11.4333
  String = P
  Tracking = 0
FEATURE [Part::Part2DObjectPython] ShapeString107  # Draft 2D object (typed FeaturePython)
  FontFile = <userpath>/Dropbox/Hobby/wordclock_git/hardware/lettering_plates/fonts/LiberationMono-Regular-stencil.ttf
  Placement = pos=(160.464,43.2409,0) rot=(0,0,1;0rad)
  Size = 11.4333
  String = R
  Tracking = 0
FEATURE [Part::Part2DObjectPython] ShapeString108  # Draft 2D object (typed FeaturePython)
  FontFile = <userpath>/Dropbox/Hobby/wordclock_git/hardware/lettering_plates/fonts/LiberationMono-Regular-stencil.ttf
  Placement = pos=(177.13,43.2409,0) rot=(0,0,1;0rad)
  Size = 11.4333
  String = M
  Tracking = 0
FEATURE [Part::Part2DObjectPython] ShapeString109  # Draft 2D object (typed FeaturePython)
  FontFile = <userpath>/Dropbox/Hobby/wordclock_git/hardware/lettering_plates/fonts/LiberationMono-Regular-stencil.ttf
  Placement = pos=(193.797,43.2409,0) rot=(0,0,1;0rad)
  Size = 11.4333
  String = W
  Tracking = 0
FEATURE [Part::Part2DObjectPython] ShapeString110  # Draft 2D object (typed FeaturePython)
  FontFile = <userpath>/Dropbox/Hobby/wordclock_git/hardware/lettering_plates/fonts/LiberationMono-Regular-stencil.ttf
  Placement = pos=(27.1303,26.5742,0) rot=(0,0,1;0rad)
  Size = 11.4333
  String = A
  Tracking = 0
FEATURE [Part::Part2DObjectPython] ShapeString111  # Draft 2D object (typed FeaturePython)
  FontFile = <userpath>/Dropbox/Hobby/wordclock_git/hardware/lettering_plates/fonts/LiberationMono-Regular-stencil.ttf
  Placement = pos=(43.797,26.5742,0) rot=(0,0,1;0rad)
  Size = 11.4333
  String = L
  Tracking = 0
FEATURE [Part::Part2DObjectPython] ShapeString112  # Draft 2D object (typed FeaturePython)
  FontFile = <userpath>/Dropbox/Hobby/wordclock_git/hardware/lettering_plates/fonts/LiberationMono-Regular-stencil.ttf
  Placement = pos=(60.4637,26.5742,0) rot=(0,0,1;0rad)
  Size = 11.4333
  String = G
  Tracking = 0
FEATURE [Part::Part2DObjectPython] ShapeString113  # Draft 2D object (typed FeaturePython)
  FontFile = <userpath>/Dropbox/Hobby/wordclock_git/hardware/lettering_plates/fonts/LiberationMono-Regular-stencil.ttf
  Placement = pos=(77.1303,26.5742,0) rot=(0,0,1;0rad)
  Size = 11.4333
  String = E
  Tracking = 0
FEATURE [Part::Part2DObjectPython] ShapeString114  # Draft 2D object (typed FeaturePython)
  FontFile = <userpath>/Dropbox/Hobby/wordclock_git/hardware/lettering_plates/fonts/LiberationMono-Regular-stencil.ttf
  Placement = pos=(93.797,26.5742,0) rot=(0,0,1;0rad)
  Size = 11.4333
  String = W
  Tracking = 0
FEATURE [Part::Part2DObjectPython] ShapeString115  # Draft 2D object (typed FeaturePython)
  FontFile = <userpath>/Dropbox/Hobby/wordclock_git/hardware/lettering_plates/fonts/LiberationMono-Regular-stencil.ttf
  Placement = pos=(110.464,26.5742,0) rot=(0,0,1;0rad)
  Size = 11.4333
  String = E
  Tracking = 0
FEATURE [Part::Part2DObjectPython] ShapeString116  # Draft 2D object (typed FeaturePython)
  FontFile = <userpath>/Dropbox/Hobby/wordclock_git/hardware/lettering_plates/fonts/LiberationMono-Regular-stencil.ttf
  Placement = pos=(127.13,26.5742,0) rot=(0,0,1;0rad)
  Size = 11.4333
  String = E
  Tracking = 0
FEATURE [Part::Part2DObjectPython] ShapeString117  # Draft 2D object (typed FeaturePython)
  FontFile = <userpath>/Dropbox/Hobby/wordclock_git/hardware/lettering_plates/fonts/LiberationMono-Regular-stencil.ttf
  Placement = pos=(143.797,26.5742,0) rot=(0,0,1;0rad)
  Size = 11.4333
  String = S
  Tracking = 0
FEATURE [Part::Part2DObjectPython] ShapeString118  # Draft 2D object (typed FeaturePython)
  FontFile = <userpath>/Dropbox/Hobby/wordclock_git/hardware/lettering_plates/fonts/LiberationMono-Regular-stencil.ttf
  Placement = pos=(160.464,26.5742,0) rot=(0,0,1;0rad)
  Size = 11.4333
  String = T
  Tracking = 0
FEATURE [Part::Part2DObjectPython] ShapeString119  # Draft 2D object (typed FeaturePython)
  FontFile = <userpath>/Dropbox/Hobby/wordclock_git/hardware/lettering_plates/fonts/LiberationMono-Regular-stencil.ttf
  Placement = pos=(177.13,26.5742,0) rot=(0,0,1;0rad)
  Size = 11.4333
  String = K
  Tracking = 0
FEATURE [Part::Part2DObjectPython] ShapeString120  # Draft 2D object (typed FeaturePython)
  FontFile = <userpath>/Dropbox/Hobby/wordclock_git/hardware/lettering_plates/fonts/LiberationMono-Regular-stencil.ttf
  Placement = pos=(193.797,26.5742,0) rot=(0,0,1;0rad)
  Size = 11.4333
  String = P
  Tracking = 0
FEATURE [Part::Part2DObjectPython] Rectangle  # Draft 2D object (typed FeaturePython)
  ChamferSize = 0
  Columns = 1
  FilletRadius = 0
  Height = 230
  Length = 230
  MakeFace = true
  Rows = 1
FEATURE [App::Part] Part
  Group = -> [Circle,ShapeString,ShapeString001,ShapeString002,ShapeString003,ShapeString004,ShapeString005,ShapeString006,ShapeString007,ShapeString008,ShapeString009,ShapeString010,ShapeString011,ShapeString012,ShapeString013,ShapeString014,ShapeString015,ShapeString016,ShapeString017,ShapeString018,ShapeString019,ShapeString020,ShapeString021,ShapeString022,ShapeString023,ShapeString024,ShapeString025,+96 more]
  Origin = -> Origin001
